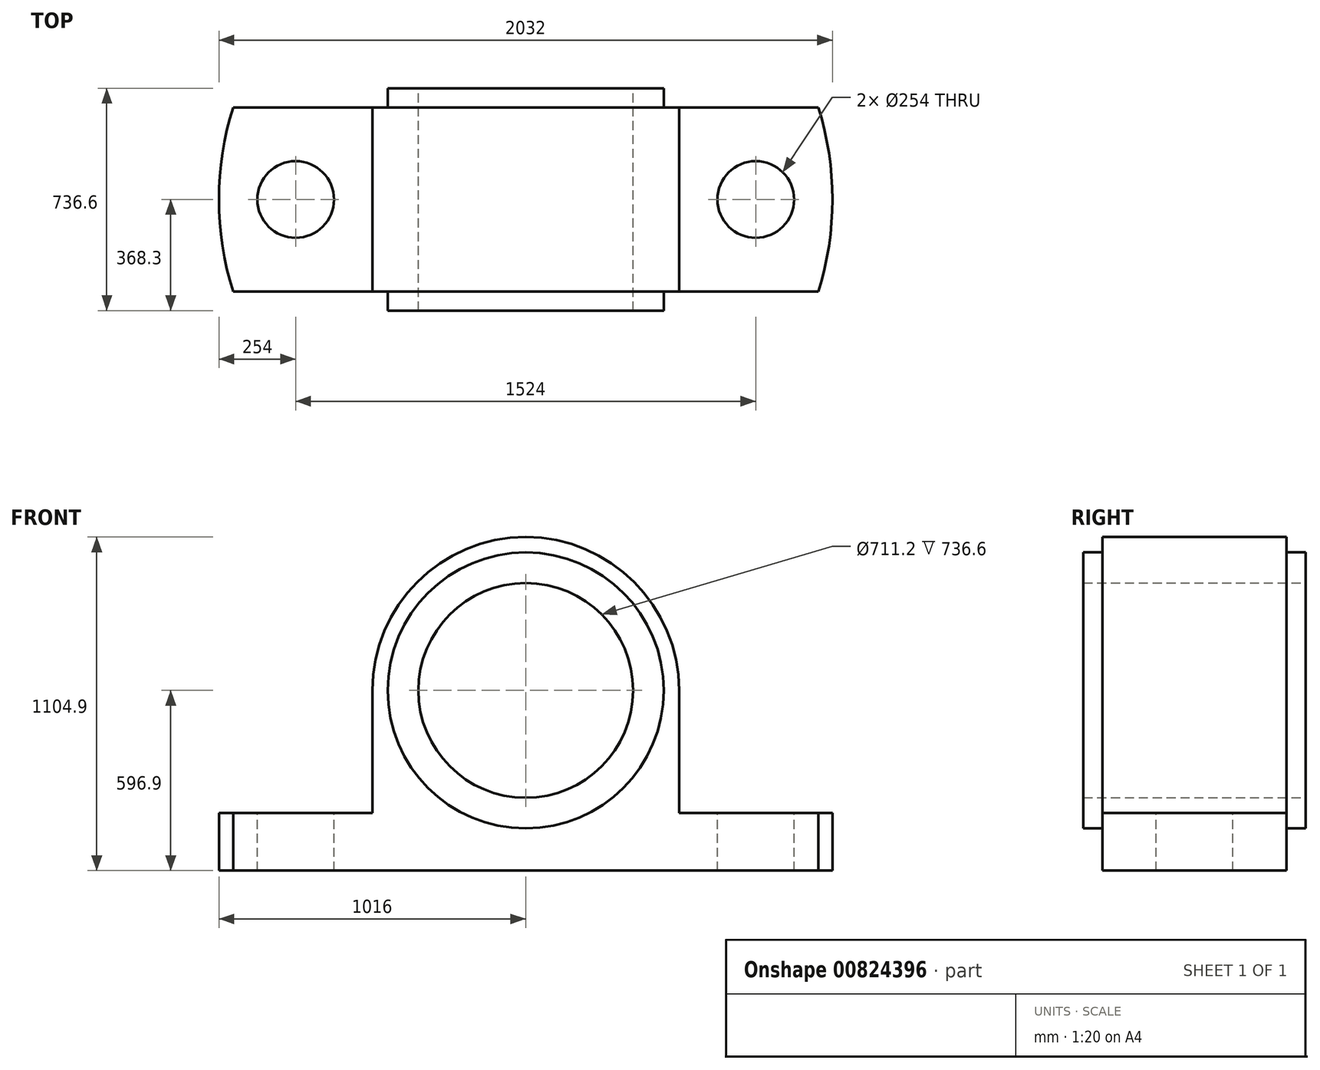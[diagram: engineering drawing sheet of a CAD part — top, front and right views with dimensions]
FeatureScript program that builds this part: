
annotation { "Feature Type Name" : "Feature", "Feature Type Description" : "" }
export const myFeature = defineFeature(function(context is Context, id is Id, definition is map)
    precondition{}
    {
        {
            var Q0;
            Q0=qCreatedBy(makeId("Front.planeOp"),FACE);
            var sketch = newSketch(context, id + "F0", { "sketchPlane" : qUnion([Q0])});
            skArc(sketch, "E0", {"start": v(508, 0) * mm, "mid": v(0, 508) * mm, "end": v(-508, 0) * mm});
            skCircle(sketch, "E1", {"center": v(0, 0) * mm, "radius": 457.2 * mm});
            skCircle(sketch, "E2", {"center": v(0, 0) * mm, "radius": 355.6 * mm});
            skLineSegment(sketch, "E3", {"start": v(-508, 0) * mm, "end": v(508, 0) * mm});
            skLineSegment(sketch, "E4", {"start": v(0, 508) * mm, "end": v(0, -508) * mm});
            skLineSegment(sketch, "E5.0", {"start": v(-1016, -596.9) * mm, "end": v(1016, -596.9) * mm});
            skLineSegment(sketch, "E6.0", {"start": v(-1016, -406.4) * mm, "end": v(-508, -406.4) * mm});
            skPoint(sketch, "E7", {"position": v(0, -406.4) * mm});
            skPoint(sketch, "E8", {"position": v(0, -596.9) * mm});
            skLineSegment(sketch, "E9", {"start": v(-1016, -406.4) * mm, "end": v(-1016, -596.9) * mm});
            skLineSegment(sketch, "E10", {"start": v(1016, -406.4) * mm, "end": v(1016, -596.9) * mm});
            skLineSegment(sketch, "E11", {"start": v(-508, 0) * mm, "end": v(-508, -406.4) * mm});
            skLineSegment(sketch, "E12", {"start": v(508, 0) * mm, "end": v(508, -406.4) * mm});
            skLineSegment(sketch, "E13.trimOffspring", {"start": v(508, -406.4) * mm, "end": v(1016, -406.4) * mm});
            skSolve(sketch);
        }
        {
            var Q0;
            Q0 = qSketchRegion(id + "F0", true);
            extrude(context, id + "F1", {"entities" : qUnion([Q0]), "endBound" : BoundingType.SYMMETRIC, "depth" : 609.6 * mm, "offsetDistance" : 25.4 * mm});
        }
        {
            var Q0;
            {var subQ0=sQuery(id+"F0.wireOp",EDGE,"E4");var subQ1=sQuery(id+"F0.wireOp",EDGE,"E1");var subQ2=makeQuery(id+"F0.imprint","INTERSECT",VERTEX,{"disambiguationData":[OD(1.0)],"derivedFrom":[subQ1,subQ0]});Q0=makeQuery(id+"F0.imprint","IMPRINT",FACE,{"disambiguationData":[TD([[makeQuery(id+"F0.imprint","IMPRINT",EDGE,{"disambiguationData":[TD([[subQ2,-1.0]])],"derivedFrom":subQ1}),1.0]])]});}
            var Q1;
            {var subQ0=sQuery(id+"F0.wireOp",EDGE,"E4");var subQ1=sQuery(id+"F0.wireOp",EDGE,"E1");var subQ2=makeQuery(id+"F0.imprint","INTERSECT",VERTEX,{"disambiguationData":[OD(1.0)],"derivedFrom":[subQ1,subQ0]});Q1=makeQuery(id+"F0.imprint","IMPRINT",FACE,{"disambiguationData":[TD([[makeQuery(id+"F0.imprint","IMPRINT",EDGE,{"disambiguationData":[TD([[subQ2,1.0]])],"derivedFrom":subQ1}),1.0]])]});}
            var Q2;
            {var subQ0=sQuery(id+"F0.wireOp",EDGE,"E4");var subQ1=sQuery(id+"F0.wireOp",EDGE,"E1");var subQ2=makeQuery(id+"F0.imprint","INTERSECT",VERTEX,{"disambiguationData":[OD(0.0)],"derivedFrom":[subQ1,subQ0]});Q2=makeQuery(id+"F0.imprint","IMPRINT",FACE,{"disambiguationData":[TD([[makeQuery(id+"F0.imprint","IMPRINT",EDGE,{"disambiguationData":[TD([[subQ2,-1.0]])],"derivedFrom":subQ1}),1.0]])]});}
            var Q3;
            {var subQ0=sQuery(id+"F0.wireOp",EDGE,"E4");var subQ1=sQuery(id+"F0.wireOp",EDGE,"E1");var subQ2=makeQuery(id+"F0.imprint","INTERSECT",VERTEX,{"disambiguationData":[OD(0.0)],"derivedFrom":[subQ1,subQ0]});Q3=makeQuery(id+"F0.imprint","IMPRINT",FACE,{"disambiguationData":[TD([[makeQuery(id+"F0.imprint","IMPRINT",EDGE,{"disambiguationData":[TD([[subQ2,1.0]])],"derivedFrom":subQ1}),1.0]])]});}
            extrude(context, id + "F2", {"entities" : qUnion([Q0, Q1, Q2, Q3]), "operationType" : NewBodyOperationType.ADD, "endBound" : BoundingType.SYMMETRIC, "depth" : 736.6 * mm, "offsetDistance" : 25.4 * mm});
        }
        {
            var Q0;
            Q0=makeQuery(id+"F1.opExtrude","SWEPT_FACE",FACE,{"disambiguationData":[OSD([sQuery(id+"F0.wireOp",EDGE,"E6.0")])]});
            var sketch = newSketch(context, id + "F3", { "sketchPlane" : qUnion([Q0])});
            skCircle(sketch, "E14", {"center": v(-762, 0) * mm, "radius": 127 * mm});
            skPoint(sketch, "E14.centerSnap0", {"position": v(-762, 304.8) * mm});
            skPoint(sketch, "E14.centerSnap1", {"position": v(-1016, 0) * mm});
            skArc(sketch, "E15", {"start": v(-969.2, 304.8) * mm, "mid": v(-1016, 0) * mm, "end": v(-969.2, -304.8) * mm});
            skSolve(sketch);
        }
        {
            var Q0;
            Q0 = qSketchRegion(id + "F3", true);
            var Q1;
            {var subQ0=sQuery(id+"F3.wireOp",EDGE,"E15");var subQ1=sQuery(id+"F0.wireOp",EDGE,"E6.0");var subQ2=makeQuery(id+"F1.opExtrude","CAP_EDGE",EDGE,{"disambiguationData":[OSD([subQ1])],"isStart":false});var subQ3=makeQuery(id+"F3.imprint","INTERSECT",VERTEX,{"derivedFrom":[subQ2,subQ0]});Q1=makeQuery(id+"F3.imprint","IMPRINT",FACE,{"disambiguationData":[TD([[makeQuery(id+"F3.imprint","IMPRINT",EDGE,{"disambiguationData":[TD([[subQ3,1.0]])],"derivedFrom":subQ0}),-1.0]])]});}
            var Q2;
            {var subQ0=sQuery(id+"F3.wireOp",EDGE,"E15");var subQ1=sQuery(id+"F0.wireOp",EDGE,"E6.0");var subQ2=makeQuery(id+"F1.opExtrude","CAP_EDGE",EDGE,{"disambiguationData":[OSD([subQ1])],"isStart":true});var subQ3=makeQuery(id+"F3.imprint","INTERSECT",VERTEX,{"derivedFrom":[subQ2,subQ0]});Q2=makeQuery(id+"F3.imprint","IMPRINT",FACE,{"disambiguationData":[TD([[makeQuery(id+"F3.imprint","IMPRINT",EDGE,{"disambiguationData":[TD([[subQ3,-1.0]])],"derivedFrom":subQ0}),-1.0]])]});}
            extrude(context, id + "F4", {"entities" : qUnion([Q0, Q1, Q2]), "operationType" : NewBodyOperationType.REMOVE, "oppositeDirection" : true, "depth" : 596.9 * mm, "offsetDistance" : 25.4 * mm});
        }
        {
            var Q0;
            Q0=makeQuery(id+"F1.opExtrude","SWEPT_FACE",FACE,{"disambiguationData":[OSD([sQuery(id+"F0.wireOp",EDGE,"E13.trimOffspring")])]});
            var sketch = newSketch(context, id + "F5", { "sketchPlane" : qUnion([Q0])});
            skCircle(sketch, "E16", {"center": v(762, 0) * mm, "radius": 127 * mm});
            skPoint(sketch, "E16.centerSnap0", {"position": v(1016, 0) * mm});
            skPoint(sketch, "E16.centerSnap1", {"position": v(762, 304.8) * mm});
            skArc(sketch, "E17", {"start": v(969.2, -304.8) * mm, "mid": v(1016, 0) * mm, "end": v(969.2, 304.8) * mm});
            skSolve(sketch);
        }
        {
            var Q0;
            {var subQ0=sQuery(id+"F5.wireOp",EDGE,"E17");var subQ1=sQuery(id+"F0.wireOp",EDGE,"E13.trimOffspring");var subQ2=makeQuery(id+"F1.opExtrude","CAP_EDGE",EDGE,{"disambiguationData":[OSD([subQ1])],"isStart":true});var subQ3=makeQuery(id+"F5.imprint","INTERSECT",VERTEX,{"derivedFrom":[subQ2,subQ0]});Q0=makeQuery(id+"F5.imprint","IMPRINT",FACE,{"disambiguationData":[TD([[makeQuery(id+"F5.imprint","IMPRINT",EDGE,{"disambiguationData":[TD([[subQ3,1.0]])],"derivedFrom":subQ0}),-1.0]])]});}
            var Q1;
            {var subQ0=sQuery(id+"F5.wireOp",EDGE,"E17");var subQ1=sQuery(id+"F0.wireOp",EDGE,"E13.trimOffspring");var subQ2=makeQuery(id+"F1.opExtrude","CAP_EDGE",EDGE,{"disambiguationData":[OSD([subQ1])],"isStart":false});var subQ3=makeQuery(id+"F5.imprint","INTERSECT",VERTEX,{"derivedFrom":[subQ2,subQ0]});Q1=makeQuery(id+"F5.imprint","IMPRINT",FACE,{"disambiguationData":[TD([[makeQuery(id+"F5.imprint","IMPRINT",EDGE,{"disambiguationData":[TD([[subQ3,-1.0]])],"derivedFrom":subQ0}),-1.0]])]});}
            var Q2;
            Q2=makeQuery(id+"F5.imprint","IMPRINT",FACE,{"disambiguationData":[TD([[makeQuery(id+"F5.imprint","IMPRINT",EDGE,{"derivedFrom":sQuery(id+"F5.wireOp",EDGE,"E16")}),1.0]])]});
            extrude(context, id + "F6", {"entities" : qUnion([Q0, Q1, Q2]), "operationType" : NewBodyOperationType.REMOVE, "endBound" : BoundingType.THROUGH_ALL, "oppositeDirection" : true, "depth" : 25.4 * mm, "offsetDistance" : 25.4 * mm});
        }
    });
